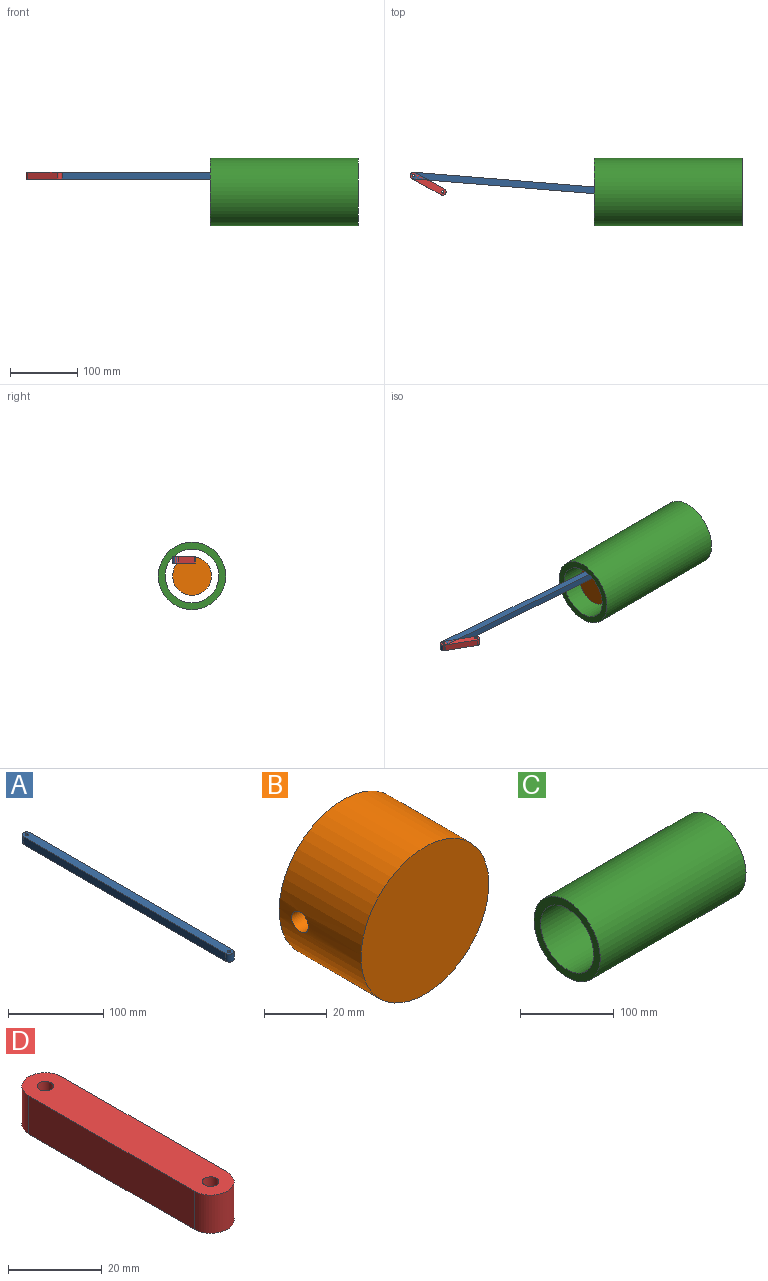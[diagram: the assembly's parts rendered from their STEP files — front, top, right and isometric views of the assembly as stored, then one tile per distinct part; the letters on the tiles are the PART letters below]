
ASSEMBLY  parts=4 mates=3
PART A: 8 faces, bbox 10x310x10 mm
  f0: plane 300x10mm, normal (-1,0,0), area 3000mm2, adj f1,f4,f6,f7
  f1: cylinder r=5mm len=10mm, axis (0,0,-1), area 157.1mm2, adj f0,f2,f6,f7
  f2: plane 300x10mm, normal (1,0,0), area 3000mm2, adj f1,f4,f6,f7
  f3: cylinder r=1.73mm len=10mm, axis (0,0,-1), area 108.8mm2, adj f6,f7
  f4: cylinder r=5mm len=10mm, axis (0,0,-1), area 157.1mm2, adj f0,f2,f6,f7
  f5: cylinder r=1.78mm len=10mm, axis (0,0,-1), area 111.8mm2, adj f6,f7
  f6: plane 310x10mm, normal (0,0,1), area 3059.2mm2, adj f0,f1,f2,f3,f4,f5
  f7: plane 310x10mm, normal (0,0,-1), area 3059.2mm2, adj f0,f1,f2,f3,f4,f5
PART B: 4 faces, bbox 57.5x36.9x57.5 mm
  f0: cylinder r=28.76mm len=57.53mm, axis (0,1,0), area 6578.8mm2, adj f1,f2,f3
  f1: plane 57.53x57.53mm, normal (0,-1,0), area 2599.1mm2, adj f0
  f2: plane 57.53x57.53mm, normal (0,1,0), area 2599.1mm2, adj f0
  f3: cylinder r=3.78mm len=57.53mm, axis (-1,0,0), area 1359.9mm2, adj f0
PART C: 4 faces, bbox 220x100x100 mm
  f0: cylinder r=40mm len=220mm, axis (-1,0,0), area 55292mm2, adj f2,f3
  f1: cylinder r=50mm len=220mm, axis (-1,0,0), area 69115mm2, adj f2,f3
  f2: plane 100x100mm, normal (1,0,0), area 2827.4mm2, adj f0,f1
  f3: plane 100x100mm, normal (-1,0,0), area 2827.4mm2, adj f0,f1
PART D: 8 faces, bbox 10x60x10 mm
  f0: plane 50x10mm, normal (-1,0,0), area 500mm2, adj f1,f4,f6,f7
  f1: cylinder r=5mm len=10mm, axis (0,0,-1), area 157.1mm2, adj f0,f2,f6,f7
  f2: plane 50x10mm, normal (1,0,0), area 500mm2, adj f1,f4,f6,f7
  f3: cylinder r=1.73mm len=10mm, axis (0,0,-1), area 108.8mm2, adj f6,f7
  f4: cylinder r=5mm len=10mm, axis (0,0,-1), area 157.1mm2, adj f0,f2,f6,f7
  f5: cylinder r=1.78mm len=10mm, axis (0,0,-1), area 111.8mm2, adj f6,f7
  f6: plane 60x10mm, normal (0,0,1), area 559.2mm2, adj f0,f1,f2,f3,f4,f5
  f7: plane 60x10mm, normal (0,0,-1), area 559.2mm2, adj f0,f1,f2,f3,f4,f5
PLACE A rot(axis=(0,0,1),85.3deg) t=(-44.07,19.39,-10)mm
PLACE B rot(axis=(0.58,-0.58,0.58),120deg) t=(246.05,0,-29.11)mm
PLACE C t=(225.03,0,-29.11)mm
PLACE D rot(axis=(0,0,1),60.8deg) t=(-46.1,20,-10)mm
MATE slider B.f0 <-> C.f0  axis (-1,0,0) through (264.5,0,-29.11)mm
MATE revolute A.f3 <-> D.f3  axis (0,0,1) through (-43.66,24.37,0)mm
MATE revolute A.f1 <-> B.f3  axis (0,0,1) through (255.35,0,0)mm
